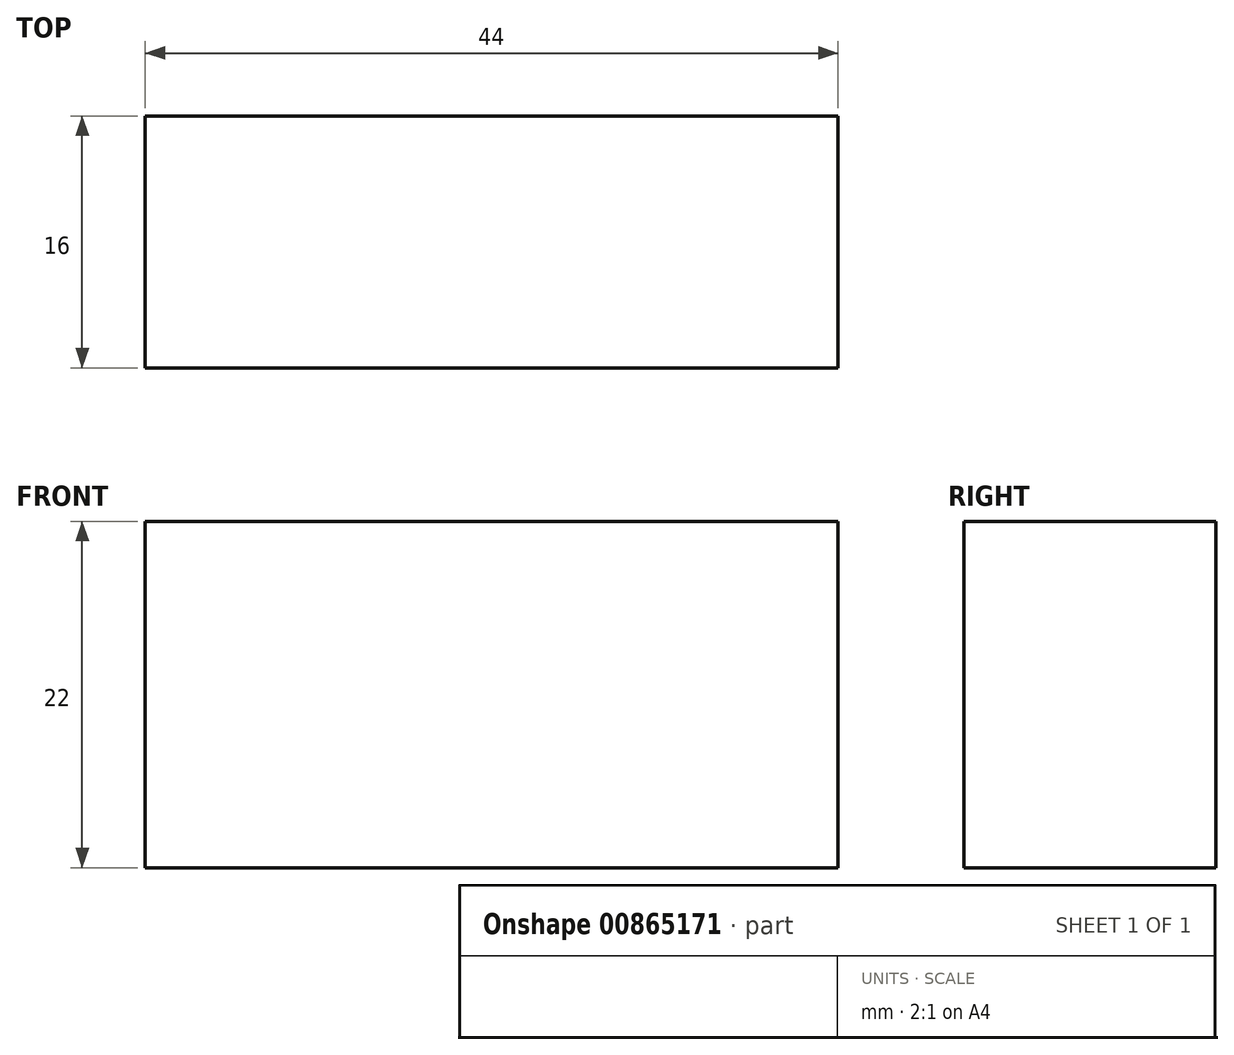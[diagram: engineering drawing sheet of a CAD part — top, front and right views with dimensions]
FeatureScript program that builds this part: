
annotation { "Feature Type Name" : "Feature", "Feature Type Description" : "" }
export const myFeature = defineFeature(function(context is Context, id is Id, definition is map)
    precondition{}
    {
        {
            var Q0;
            Q0=qCreatedBy(makeId("Top.planeOp"),FACE);
            var sketch = newSketch(context, id + "F0", { "sketchPlane" : qUnion([Q0])});
            skLineSegment(sketch, "E0.bottom", {"start": v(-22.15, 4.56) * mm, "end": v(21.85, 4.56) * mm});
            skLineSegment(sketch, "E0.top", {"start": v(-22.15, -11.44) * mm, "end": v(21.85, -11.44) * mm});
            skLineSegment(sketch, "E0.left", {"start": v(-22.15, 4.56) * mm, "end": v(-22.15, -11.44) * mm});
            skLineSegment(sketch, "E0.right", {"start": v(21.85, 4.56) * mm, "end": v(21.85, -11.44) * mm});
            skSolve(sketch);
        }
        {
            var Q0;
            Q0 = qSketchRegion(id + "F0", true);
            extrude(context, id + "F1", {"entities" : qUnion([Q0]), "depth" : 22 * mm, "offsetDistance" : 25.4 * mm});
        }
    });
